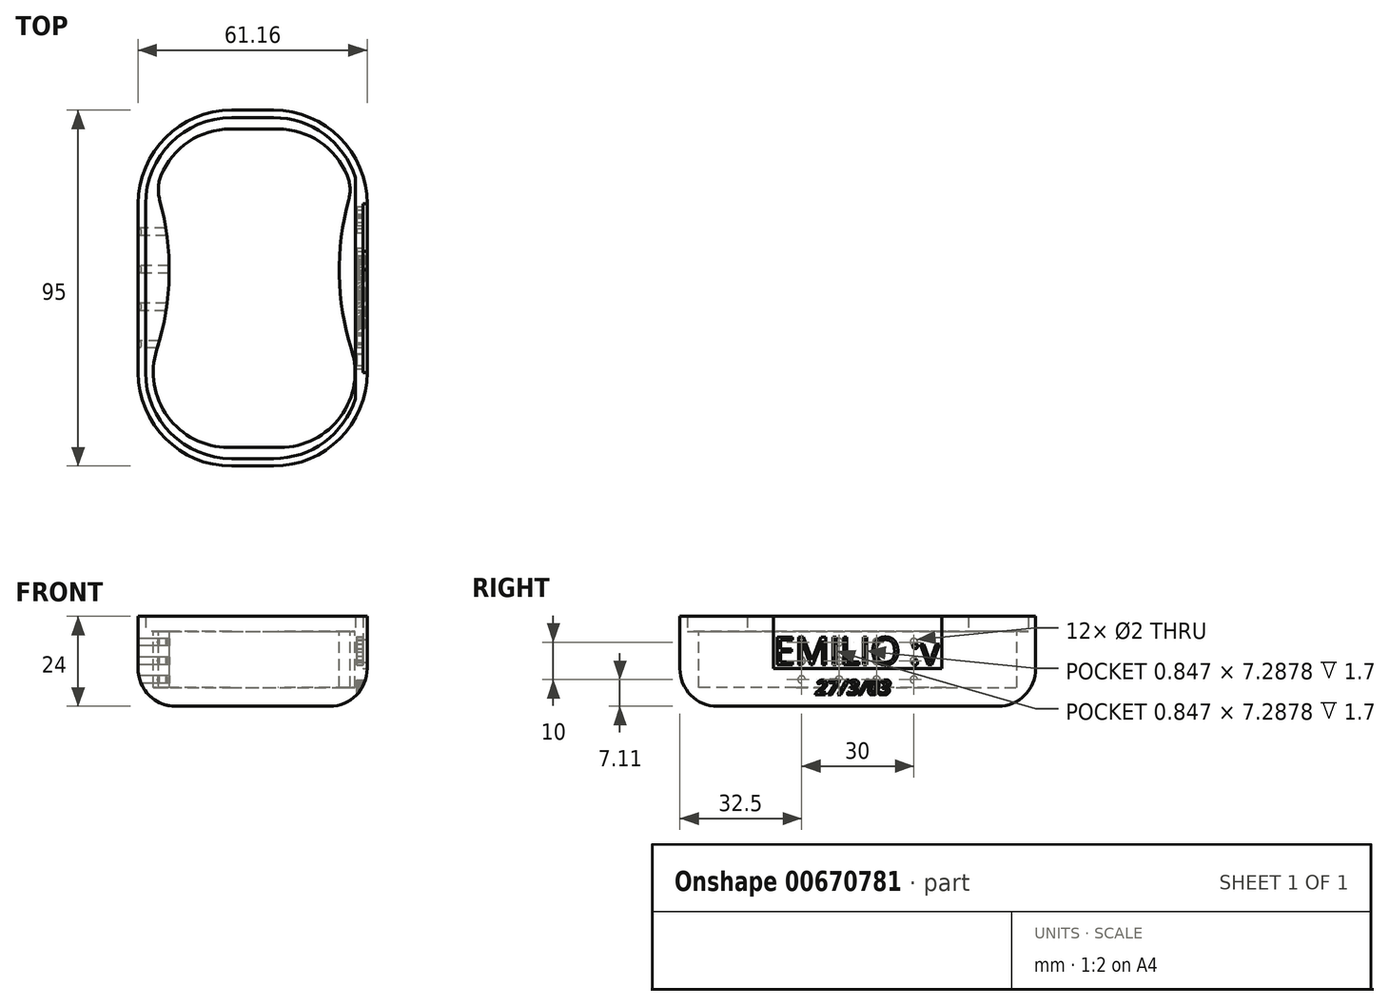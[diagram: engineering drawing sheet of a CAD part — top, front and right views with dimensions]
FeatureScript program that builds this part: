
annotation { "Feature Type Name" : "Feature", "Feature Type Description" : "" }
export const myFeature = defineFeature(function(context is Context, id is Id, definition is map)
    precondition{}
    {
        {
            var Q0;
            Q0=qCreatedBy(makeId("Top.planeOp"),FACE);
            var sketch = newSketch(context, id + "F0", { "sketchPlane" : qUnion([Q0])});
            skLineSegment(sketch, "E0", {"start": v(-100, 0) * mm, "end": v(100, 0) * mm, "construction": true});
            skLineSegment(sketch, "E1", {"start": v(0, 100) * mm, "end": v(0, -100) * mm, "construction": true});
            skLineSegment(sketch, "E2.bottom", {"start": v(19.66, 85) * mm, "end": v(32.34, 85) * mm});
            skLineSegment(sketch, "E2.top", {"start": v(19.05, 0) * mm, "end": v(32.95, 0) * mm});
            skPoint(sketch, "E3.visualSharp", {"position": v(0, 85) * mm});
            skArc(sketch, "E3.filletArc", {"start": v(19.66, 85) * mm, "mid": v(8.5, 81.6) * mm, "end": v(1.13, 72.53) * mm});
            skPoint(sketch, "E4.visualSharp", {"position": v(52, 85) * mm});
            skArc(sketch, "E4.filletArc", {"start": v(50.87, 72.53) * mm, "mid": v(43.5, 81.6) * mm, "end": v(32.34, 85) * mm});
            skPoint(sketch, "E5.visualSharp", {"position": v(52, 0) * mm});
            skArc(sketch, "E5.filletArc", {"start": v(32.95, 0) * mm, "mid": v(49.1, 8.2) * mm, "end": v(52, 26.08) * mm});
            skPoint(sketch, "E6.visualSharp", {"position": v(0, 0) * mm});
            skArc(sketch, "E6.filletArc", {"start": v(0, 26.08) * mm, "mid": v(2.9, 8.2) * mm, "end": v(19.05, 0) * mm});
            skArc(sketch, "E7", {"start": v(51.24, 66.09) * mm, "mid": v(48.7, 46.03) * mm, "end": v(52, 26.08) * mm});
            skArc(sketch, "E8", {"start": v(0, 26.08) * mm, "mid": v(3.3, 46.03) * mm, "end": v(0.76, 66.09) * mm});
            skPoint(sketch, "E9.visualSharp", {"position": v(52, 68.65) * mm});
            skArc(sketch, "E9.filletArc", {"start": v(51.24, 66.09) * mm, "mid": v(51.58, 69.34) * mm, "end": v(50.87, 72.53) * mm});
            skPoint(sketch, "E10.visualSharp", {"position": v(0, 68.65) * mm});
            skArc(sketch, "E10.filletArc", {"start": v(1.13, 72.53) * mm, "mid": v(0.42, 69.34) * mm, "end": v(0.76, 66.09) * mm});
            skSolve(sketch);
        }
        {
            var Q0;
            Q0 = qSketchRegion(id + "F0", true);
            extrude(context, id + "F1", {"entities" : qUnion([Q0]), "oppositeDirection" : true, "depth" : 15 * mm, "offsetDistance" : 25 * mm});
        }
        {
            var Q0;
            Q0=qCreatedBy(makeId("Top.planeOp"),FACE);
            cPlane(context, id + "F2", {"entities" : qUnion([Q0]), "cplaneType" : CPlaneType.OFFSET, "offset" : 20 * mm, "oppositeDirection" : true, "width" : 150 * mm, "height" : 150 * mm});
        }
        {
            var Q0;
            Q0=qCreatedBy(id+"F2.planeOp",FACE);
            var sketch = newSketch(context, id + "F3", { "sketchPlane" : qUnion([Q0])});
            skLineSegment(sketch, "E11.bottom", {"start": v(56.16, 90) * mm, "end": v(-5, 90) * mm});
            skLineSegment(sketch, "E11.top", {"start": v(56.16, -5) * mm, "end": v(-5, -5) * mm});
            skLineSegment(sketch, "E11.left", {"start": v(-5, -5) * mm, "end": v(-5, 90) * mm});
            skLineSegment(sketch, "E11.right", {"start": v(56.16, -5) * mm, "end": v(56.16, 90) * mm});
            skSolve(sketch);
        }
        {
            var Q0;
            Q0 = qSketchRegion(id + "F3", true);
            extrude(context, id + "F4", {"entities" : qUnion([Q0]), "depth" : 20 * mm, "offsetDistance" : 25 * mm});
        }
        {
            var Q0;
            Q0=makeQuery(id+"F1.opExtrude","SWEPT_BODY",BODY,{"disambiguationData":[OSD([sQuery(id+"F0.wireOp",EDGE,"E2.bottom"),sQuery(id+"F0.wireOp",EDGE,"E2.top"),sQuery(id+"F0.wireOp",EDGE,"E3.filletArc"),sQuery(id+"F0.wireOp",EDGE,"E4.filletArc"),sQuery(id+"F0.wireOp",EDGE,"E5.filletArc"),sQuery(id+"F0.wireOp",EDGE,"E6.filletArc"),sQuery(id+"F0.wireOp",EDGE,"E7"),sQuery(id+"F0.wireOp",EDGE,"E8"),sQuery(id+"F0.wireOp",EDGE,"E9.filletArc"),sQuery(id+"F0.wireOp",EDGE,"E10.filletArc")])]});
            var Q1;
            Q1=makeQuery(id+"F4.opExtrude","SWEPT_BODY",BODY,{"disambiguationData":[OSD([sQuery(id+"F3.wireOp",EDGE,"E11.bottom"),sQuery(id+"F3.wireOp",EDGE,"E11.top"),sQuery(id+"F3.wireOp",EDGE,"E11.left"),sQuery(id+"F3.wireOp",EDGE,"E11.right")])]});
            booleanBodies(context, id + "F5", {"operationType" : BooleanOperationType.SUBTRACTION, "tools" : qUnion([Q0]), "targets" : qUnion([Q1])});
        }
        {
            var Q0;
            Q0=makeQuery(id+"F4.opExtrude","SWEPT_EDGE",EDGE,{"disambiguationData":[OSD([sQuery(id+"F3.wireOp",EDGE,"E11.bottom"),sQuery(id+"F3.wireOp",EDGE,"E11.left")])]});
            var Q1;
            Q1=makeQuery(id+"F4.opExtrude","SWEPT_EDGE",EDGE,{"disambiguationData":[OSD([sQuery(id+"F3.wireOp",EDGE,"E11.top"),sQuery(id+"F3.wireOp",EDGE,"E11.left")])]});
            var Q2;
            Q2=makeQuery(id+"F4.opExtrude","SWEPT_EDGE",EDGE,{"disambiguationData":[OSD([sQuery(id+"F3.wireOp",EDGE,"E11.top"),sQuery(id+"F3.wireOp",EDGE,"E11.right")])]});
            var Q3;
            Q3=makeQuery(id+"F4.opExtrude","SWEPT_EDGE",EDGE,{"disambiguationData":[OSD([sQuery(id+"F3.wireOp",EDGE,"E11.bottom"),sQuery(id+"F3.wireOp",EDGE,"E11.right")])]});
            fillet(context, id + "F6", {"entities" : qUnion([Q0, Q1, Q2, Q3]), "radius" : 25 * mm, "tangentPropagation" : true, "allowEdgeOverflow" : false});
        }
        {
            var Q0;
            Q0=makeQuery(id+"F4.opExtrude","CAP_FACE",FACE,{"disambiguationData":[OSD([sQuery(id+"F3.wireOp",EDGE,"E11.bottom"),sQuery(id+"F3.wireOp",EDGE,"E11.top"),sQuery(id+"F3.wireOp",EDGE,"E11.left"),sQuery(id+"F3.wireOp",EDGE,"E11.right")])],"isStart":true});
            fillet(context, id + "F7", {"entities" : qUnion([Q0]), "radius" : 10 * mm, "tangentPropagation" : true, "allowEdgeOverflow" : false});
        }
        {
            var Q0;
            Q0=makeQuery(id+"F4.opExtrude","SWEPT_FACE",FACE,{"disambiguationData":[OSD([sQuery(id+"F3.wireOp",EDGE,"E11.right")])]});
            var sketch = newSketch(context, id + "F8", { "sketchPlane" : qUnion([Q0])});
            skText(sketch, "E12", { "text": "EMILIO :v", "fontName": "OpenSans-Regular.ttf"});
            skText(sketch, "E13", { "text": "27/3/03", "fontName": "OpenSans-BoldItalic.ttf"});
            const initialGuessF8  = {"E12": [0.02, -0.00889, 1, 0, 0.00735], "E13": [0.03128, -0.017, 1, 0, 0.004]};
            skSetInitialGuess(sketch, initialGuessF8);
            skSolve(sketch);
        }
        {
            var Q0;
            Q0=makeQuery(id+"F8.imprint","IMPRINT",FACE,{"disambiguationData":[TD([[makeQuery(id+"F8.imprint","IMPRINT",EDGE,{"derivedFrom":sQuery(id+"F8.wireOp",EDGE,"E12.sketch_text.stroke-0")}),1.0]])]});
            extrude(context, id + "F9", {"entities" : qUnion([Q0]), "operationType" : NewBodyOperationType.REMOVE, "oppositeDirection" : true, "depth" : 1.1 * mm, "offsetDistance" : 25 * mm});
        }
        {
            var Q0;
            Q0 = qSketchRegion(id + "F8", true);
            extrude(context, id + "F10", {"entities" : qUnion([Q0]), "operationType" : NewBodyOperationType.REMOVE, "oppositeDirection" : true, "depth" : 2.8 * mm, "offsetDistance" : 25 * mm});
        }
        {
            var Q0;
            Q0=makeQuery(id+"F4.opExtrude","SWEPT_FACE",FACE,{"disambiguationData":[OSD([sQuery(id+"F3.wireOp",EDGE,"E11.left")])]});
            var sketch = newSketch(context, id + "F11", { "sketchPlane" : qUnion([Q0])});
            skCircle(sketch, "E14", {"center": v(-57.5, -12.89) * mm, "radius": 1 * mm});
            skCircle(sketch, "E15.0.1.0", {"center": v(-57.5, -7.89) * mm, "radius": 1 * mm});
            skCircle(sketch, "E15.0.2.0", {"center": v(-57.5, -2.89) * mm, "radius": 1 * mm});
            skCircle(sketch, "E15.1.0.0", {"center": v(-47.5, -12.89) * mm, "radius": 1 * mm});
            skCircle(sketch, "E15.1.1.0", {"center": v(-47.5, -7.89) * mm, "radius": 1 * mm});
            skCircle(sketch, "E15.1.2.0", {"center": v(-47.5, -2.89) * mm, "radius": 1 * mm});
            skCircle(sketch, "E15.2.0.0", {"center": v(-37.5, -12.89) * mm, "radius": 1 * mm});
            skCircle(sketch, "E15.2.1.0", {"center": v(-37.5, -7.89) * mm, "radius": 1 * mm});
            skCircle(sketch, "E15.2.2.0", {"center": v(-37.5, -2.89) * mm, "radius": 1 * mm});
            skCircle(sketch, "E15.3.0.0", {"center": v(-27.5, -12.89) * mm, "radius": 1 * mm});
            skCircle(sketch, "E15.3.1.0", {"center": v(-27.5, -7.89) * mm, "radius": 1 * mm});
            skCircle(sketch, "E15.3.2.0", {"center": v(-27.5, -2.89) * mm, "radius": 1 * mm});
            skLineSegment(sketch, "E15.direction1", {"start": v(-57.5, -12.89) * mm, "end": v(-47.5, -12.89) * mm, "construction": true});
            skLineSegment(sketch, "E15.direction2", {"start": v(-57.5, -12.89) * mm, "end": v(-57.5, -7.89) * mm, "construction": true});
            skSolve(sketch);
        }
        {
            var Q0;
            Q0 = qSketchRegion(id + "F11", true);
            extrude(context, id + "F12", {"entities" : qUnion([Q0]), "operationType" : NewBodyOperationType.REMOVE, "oppositeDirection" : true, "depth" : 25 * mm, "offsetDistance" : 25 * mm});
        }
        {
            var Q0;
            Q0=makeQuery(id+"F4.opExtrude","CAP_FACE",FACE,{"disambiguationData":[OSD([sQuery(id+"F3.wireOp",EDGE,"E11.bottom"),sQuery(id+"F3.wireOp",EDGE,"E11.top"),sQuery(id+"F3.wireOp",EDGE,"E11.left"),sQuery(id+"F3.wireOp",EDGE,"E11.right")])],"isStart":false});
            var sketch = newSketch(context, id + "F13", { "sketchPlane" : qUnion([Q0])});
            skArc(sketch, "E16.0", {"start": v(31.16, -3) * mm, "mid": v(44.72, 1.42) * mm, "end": v(53.06, 12.97) * mm});
            skLineSegment(sketch, "E16.1", {"start": v(20, -3) * mm, "end": v(31.16, -3) * mm});
            skLineSegment(sketch, "E16.2", {"start": v(53.06, 12.97) * mm, "end": v(53.06, 72.03) * mm});
            skArc(sketch, "E16.3", {"start": v(-3, 20) * mm, "mid": v(3.74, 3.74) * mm, "end": v(20, -3) * mm});
            skArc(sketch, "E16.4", {"start": v(53.06, 72.03) * mm, "mid": v(44.72, 83.58) * mm, "end": v(31.16, 88) * mm});
            skLineSegment(sketch, "E16.5", {"start": v(31.16, 88) * mm, "end": v(20, 88) * mm});
            skArc(sketch, "E16.6", {"start": v(20, 88) * mm, "mid": v(3.74, 81.26) * mm, "end": v(-3, 65) * mm});
            skLineSegment(sketch, "E16.7", {"start": v(-3, 65) * mm, "end": v(-3, 20) * mm});
            skSolve(sketch);
        }
        {
            var Q0;
            Q0=makeQuery(id+"F13.imprint","IMPRINT",FACE,{"disambiguationData":[TD([[makeQuery(id+"F13.imprint","IMPRINT",EDGE,{"derivedFrom":sQuery(id+"F13.wireOp",EDGE,"E16.0")}),-1.0]])]});
            extrude(context, id + "F14", {"entities" : qUnion([Q0]), "operationType" : NewBodyOperationType.ADD, "depth" : 4 * mm, "offsetDistance" : 25 * mm});
        }
    });
